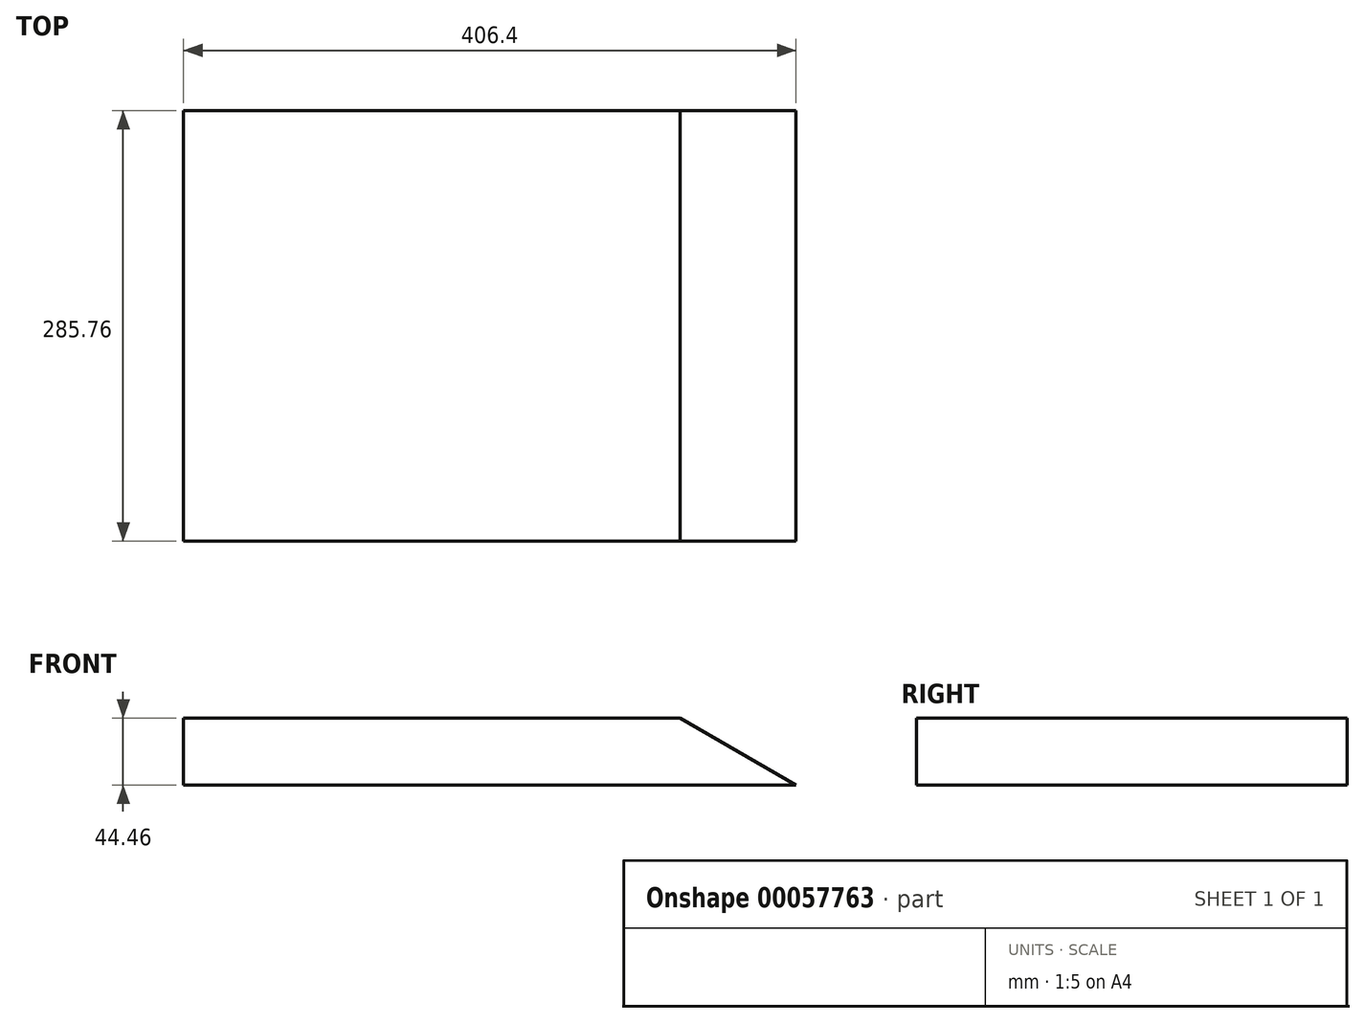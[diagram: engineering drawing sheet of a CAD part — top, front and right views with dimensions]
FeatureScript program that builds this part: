
annotation { "Feature Type Name" : "Feature", "Feature Type Description" : "" }
export const myFeature = defineFeature(function(context is Context, id is Id, definition is map)
    precondition{}
    {
        {
            var Q0;
            Q0=qCreatedBy(makeId("Right.planeOp"),FACE);
            var sketch = newSketch(context, id + "F0", { "sketchPlane" : qUnion([Q0])});
            skLineSegment(sketch, "E0.rect.bottom", {"start": v(-142.88, -22.23) * mm, "end": v(142.88, -22.23) * mm});
            skLineSegment(sketch, "E0.rect.top", {"start": v(-142.88, 22.23) * mm, "end": v(142.88, 22.23) * mm});
            skLineSegment(sketch, "E0.rect.left", {"start": v(-142.88, -22.23) * mm, "end": v(-142.88, 22.23) * mm});
            skLineSegment(sketch, "E0.rect.right", {"start": v(142.88, -22.23) * mm, "end": v(142.88, 22.23) * mm});
            skPoint(sketch, "E0.rect.middle", {"position": v(0, 0) * mm});
            skSolve(sketch);
        }
        {
            var Q0;
            Q0=makeQuery(id+"F0.imprint","IMPRINT",FACE,{"disambiguationData":[TD([[makeQuery(id+"F0.imprint","IMPRINT",EDGE,{"derivedFrom":sQuery(id+"F0.wireOp",EDGE,"E0.rect.bottom")}),1.0]])]});
            extrude(context, id + "F1", {"entities" : qUnion([Q0]), "endBound" : BoundingType.SYMMETRIC, "depth" : 406.4 * mm});
        }
        {
            var Q0;
            Q0=qCreatedBy(makeId("Front.planeOp"),FACE);
            var sketch = newSketch(context, id + "F2", { "sketchPlane" : qUnion([Q0])});
            skLineSegment(sketch, "E1", {"start": v(228.6, 47.63) * mm, "end": v(82.22, 47.63) * mm});
            skLineSegment(sketch, "E2", {"start": v(82.22, 47.63) * mm, "end": v(228.6, -36.89) * mm});
            skLineSegment(sketch, "E3", {"start": v(228.6, -36.89) * mm, "end": v(228.6, 47.63) * mm});
            skSolve(sketch);
        }
        {
            var Q0;
            Q0 = qSketchRegion(id + "F2", true);
            extrude(context, id + "F3", {"entities" : qUnion([Q0]), "operationType" : NewBodyOperationType.REMOVE, "endBound" : BoundingType.SYMMETRIC, "depth" : 406.4 * mm});
        }
    });
